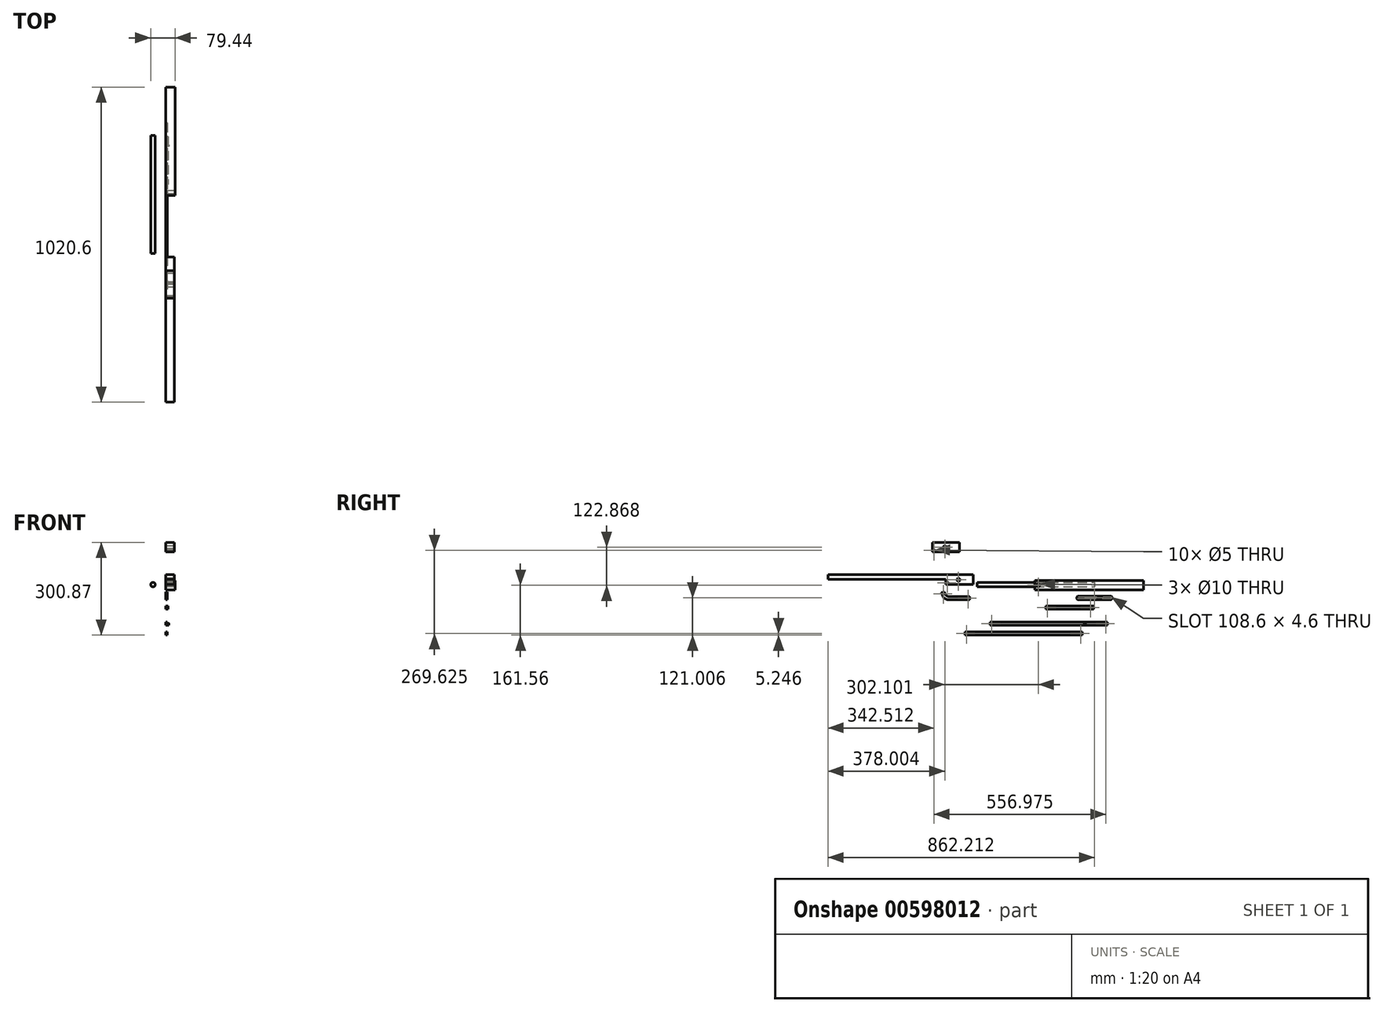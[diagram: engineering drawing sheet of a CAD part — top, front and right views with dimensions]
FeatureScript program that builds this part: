
annotation { "Feature Type Name" : "Feature", "Feature Type Description" : "" }
export const myFeature = defineFeature(function(context is Context, id is Id, definition is map)
    precondition{}
    {
        {
            var Q0;
            Q0=qCreatedBy(makeId("Right.planeOp"),FACE);
            var sketch = newSketch(context, id + "F0", { "sketchPlane" : qUnion([Q0])});
            skLineSegment(sketch, "E0.bottom", {"start": v(-194.1, 14.75) * mm, "end": v(156.9, 14.75) * mm});
            skLineSegment(sketch, "E0.top", {"start": v(-194.1, 44.75) * mm, "end": v(156.9, 44.75) * mm});
            skLineSegment(sketch, "E0.left", {"start": v(-194.1, 14.75) * mm, "end": v(-194.1, 44.75) * mm});
            skLineSegment(sketch, "E0.right", {"start": v(156.9, 14.75) * mm, "end": v(156.9, 44.75) * mm});
            skCircle(sketch, "E1", {"center": v(-183.6, 29.75) * mm, "radius": 5 * mm});
            skSolve(sketch);
        }
        {
            var Q0;
            Q0=qCreatedBy(makeId("Right.planeOp"),FACE);
            var sketch = newSketch(context, id + "F1", { "sketchPlane" : qUnion([Q0])});
            skCircle(sketch, "E2", {"center": v(-441.72, 47.74) * mm, "radius": 5 * mm});
            skLineSegment(sketch, "E3.bottom", {"start": v(-482.2, 64.18) * mm, "end": v(-393.7, 64.18) * mm});
            skLineSegment(sketch, "E3.top", {"start": v(-482.2, 33.18) * mm, "end": v(-393.7, 33.18) * mm});
            skLineSegment(sketch, "E3.left", {"start": v(-482.2, 64.18) * mm, "end": v(-482.2, 33.18) * mm});
            skLineSegment(sketch, "E3.right", {"start": v(-393.7, 64.18) * mm, "end": v(-393.7, 33.18) * mm});
            skCircle(sketch, "E4", {"center": v(-477.2, 38.18) * mm, "radius": 2.5 * mm});
            skLineSegment(sketch, "E5", {"start": v(-482.2, 64.18) * mm, "end": v(-863.7, 64.18) * mm});
            skLineSegment(sketch, "E6", {"start": v(-863.7, 64.18) * mm, "end": v(-863.7, 49.18) * mm});
            skLineSegment(sketch, "E7", {"start": v(-863.7, 49.18) * mm, "end": v(-482.2, 49.18) * mm});
            skSolve(sketch);
        }
        {
            var Q0;
            Q0=qCreatedBy(makeId("Right.planeOp"),FACE);
            var sketch = newSketch(context, id + "F2", { "sketchPlane" : qUnion([Q0])});
            skCircle(sketch, "E8", {"center": v(-410.94, -12.13) * mm, "radius": 2.5 * mm});
            skCircle(sketch, "E9", {"center": v(-490.17, 2.37) * mm, "radius": 2.5 * mm});
            skLineSegment(sketch, "E10.bottom", {"start": v(-468.94, -6.88) * mm, "end": v(-405.94, -6.88) * mm});
            skLineSegment(sketch, "E10.top", {"start": v(-468.94, -17.38) * mm, "end": v(-405.94, -17.38) * mm});
            skLineSegment(sketch, "E10.left", {"start": v(-468.94, -6.88) * mm, "end": v(-468.94, -17.38) * mm});
            skLineSegment(sketch, "E10.right", {"start": v(-405.94, -6.88) * mm, "end": v(-405.94, -17.38) * mm});
            skFitSpline(sketch, "E11", {"points": [v(-468.94, -6.88) * mm, v(-480.44, -3.93) * mm, v(-486.77, 8.58) * mm], "startDerivative": vector(-26.1, 0) * mm, "endDerivative": vector(-7.25, 24.7) * mm});
            skFitSpline(sketch, "E12.0", {"points": [v(-468.94, -17.38) * mm, v(-469.56, -17.38) * mm, v(-470.86, -17.37) * mm, v(-472.98, -17.27) * mm, v(-475.24, -17.03) * mm, v(-477.66, -16.6) * mm, v(-479.79, -16.03) * mm, v(-481.54, -15.38) * mm, v(-482.88, -14.79) * mm, v(-484.22, -14.08) * mm, v(-485.54, -13.25) * mm, v(-486.62, -12.46) * mm, v(-487.46, -11.75) * mm, v(-488.26, -11.02) * mm, v(-489.16, -10.1) * mm, v(-490.45, -8.58) * mm, v(-491.79, -6.66) * mm, v(-493.08, -4.4) * mm, v(-494.13, -2.18) * mm, v(-495, -0.04) * mm, v(-495.72, 2) * mm, v(-496.33, 3.9) * mm, v(-496.68, 5.07) * mm, v(-496.84, 5.62) * mm]});
            skLineSegment(sketch, "E13", {"start": v(-496.84, 5.62) * mm, "end": v(-486.77, 8.58) * mm});
            skSolve(sketch);
        }
        {
            var Q0;
            Q0=qCreatedBy(makeId("Right.planeOp"),FACE);
            var sketch = newSketch(context, id + "F3", { "sketchPlane" : qUnion([Q0])});
            skLineSegment(sketch, "E14.bottom", {"start": v(-3.79, -47.36) * mm, "end": v(-158.79, -47.36) * mm});
            skLineSegment(sketch, "E14.top", {"start": v(-3.79, -36.86) * mm, "end": v(-158.79, -36.86) * mm});
            skLineSegment(sketch, "E14.left", {"start": v(-3.79, -47.36) * mm, "end": v(-3.79, -36.86) * mm});
            skLineSegment(sketch, "E14.right", {"start": v(-158.79, -47.36) * mm, "end": v(-158.79, -36.86) * mm});
            skPoint(sketch, "E15.visualSharp", {"position": v(-3.79, -36.36) * mm});
            skPoint(sketch, "E16.visualSharp", {"position": v(-3.79, -47.36) * mm});
            skCircle(sketch, "E17", {"center": v(-153.79, -42.1) * mm, "radius": 2.5 * mm});
            skCircle(sketch, "E18", {"center": v(-13.79, -42.1) * mm, "radius": 2.5 * mm});
            skPoint(sketch, "E19", {"position": v(-3.79, -36.86) * mm});
            skSolve(sketch);
        }
        {
            var Q0;
            Q0=qCreatedBy(makeId("Right.planeOp"),FACE);
            var sketch = newSketch(context, id + "F4", { "sketchPlane" : qUnion([Q0])});
            skLineSegment(sketch, "E20.bottom", {"start": v(-54.3, -5.58) * mm, "end": v(51.4, -5.58) * mm});
            skLineSegment(sketch, "E20.top", {"start": v(-54.4, -16.58) * mm, "end": v(51.4, -16.58) * mm});
            skLineSegment(sketch, "E20.left", {"start": v(-59, -10.28) * mm, "end": v(-59, -11.98) * mm});
            skLineSegment(sketch, "E20.right", {"start": v(56, -10.18) * mm, "end": v(56, -11.98) * mm});
            skLineSegment(sketch, "E21", {"start": v(-53.5, -10.8) * mm, "end": v(50.5, -10.8) * mm});
            skPoint(sketch, "E22.visualSharp", {"position": v(-59, -5.58) * mm});
            skArc(sketch, "E22.filletArc", {"start": v(-54.3, -5.58) * mm, "mid": v(-57.62, -6.95) * mm, "end": v(-59, -10.28) * mm});
            skPoint(sketch, "E23.visualSharp", {"position": v(-59, -16.58) * mm});
            skArc(sketch, "E23.filletArc", {"start": v(-59, -11.98) * mm, "mid": v(-57.65, -15.23) * mm, "end": v(-54.4, -16.58) * mm});
            skPoint(sketch, "E24.visualSharp", {"position": v(56, -16.58) * mm});
            skArc(sketch, "E24.filletArc", {"start": v(51.4, -16.58) * mm, "mid": v(54.65, -15.23) * mm, "end": v(56, -11.98) * mm});
            skPoint(sketch, "E25.visualSharp", {"position": v(56, -5.58) * mm});
            skArc(sketch, "E25.filletArc", {"start": v(56, -10.18) * mm, "mid": v(54.65, -6.92) * mm, "end": v(51.4, -5.58) * mm});
            skArc(sketch, "E26.0.startCap", {"start": v(-53.5, -13.1) * mm, "mid": v(-55.8, -10.8) * mm, "end": v(-53.5, -8.5) * mm});
            skArc(sketch, "E26.0.endCap", {"start": v(50.5, -8.5) * mm, "mid": v(52.8, -10.8) * mm, "end": v(50.5, -13.1) * mm});
            skLineSegment(sketch, "E26.0.left", {"start": v(-53.5, -8.5) * mm, "end": v(50.5, -8.5) * mm});
            skLineSegment(sketch, "E26.0.right", {"start": v(-53.5, -13.1) * mm, "end": v(50.5, -13.1) * mm});
            skPoint(sketch, "E27", {"position": v(-59, -6.08) * mm});
            skSolve(sketch);
        }
        {
            var Q0;
            Q0=makeQuery(id+"F0.imprint","IMPRINT",FACE,{"disambiguationData":[TD([[makeQuery(id+"F0.imprint","IMPRINT",EDGE,{"derivedFrom":sQuery(id+"F0.wireOp",EDGE,"E0.bottom")}),1.0]])]});
            extrude(context, id + "F5", {"entities" : qUnion([Q0]), "depth" : 30 * mm, "offsetDistance" : 25 * mm});
        }
        {
            var Q0;
            Q0 = qSketchRegion(id + "F1", true);
            extrude(context, id + "F6", {"entities" : qUnion([Q0]), "depth" : 28 * mm, "offsetDistance" : 25 * mm});
        }
        {
            var Q0;
            Q0 = qSketchRegion(id + "F2", true);
            extrude(context, id + "F7", {"entities" : qUnion([Q0]), "depth" : 5 * mm, "offsetDistance" : 25 * mm});
        }
        {
            var Q0;
            Q0 = qSketchRegion(id + "F3", true);
            extrude(context, id + "F8", {"entities" : qUnion([Q0]), "depth" : 7 * mm, "offsetDistance" : 25 * mm});
        }
        {
            var Q0;
            Q0 = qSketchRegion(id + "F4", true);
            extrude(context, id + "F9", {"entities" : qUnion([Q0]), "depth" : 2 * mm, "offsetDistance" : 25 * mm});
        }
        {
            var Q0;
            Q0=qCreatedBy(makeId("Right.planeOp"),FACE);
            var sketch = newSketch(context, id + "F10", { "sketchPlane" : qUnion([Q0])});
            skCircle(sketch, "E28", {"center": v(-32.9, -96.73) * mm, "radius": 2.5 * mm});
            skSolve(sketch);
        }
        {
            var Q0;
            Q0=makeQuery(id+"F10.imprint","IMPRINT",FACE,{"disambiguationData":[TD([[makeQuery(id+"F10.imprint","IMPRINT",EDGE,{"derivedFrom":sQuery(id+"F10.wireOp",EDGE,"E28")}),1.0]])]});
            extrude(context, id + "F11", {"entities" : qUnion([Q0]), "depth" : 10 * mm, "offsetDistance" : 25 * mm});
        }
        {
            var Q0;
            Q0=qCreatedBy(makeId("Right.planeOp"),FACE);
            var sketch = newSketch(context, id + "F12", { "sketchPlane" : qUnion([Q0])});
            skLineSegment(sketch, "E29.bottom", {"start": v(40.78, -99.32) * mm, "end": v(-339.22, -99.32) * mm});
            skLineSegment(sketch, "E29.top", {"start": v(40.78, -88.82) * mm, "end": v(-339.22, -88.82) * mm});
            skLineSegment(sketch, "E29.left", {"start": v(40.78, -99.32) * mm, "end": v(40.78, -88.82) * mm});
            skLineSegment(sketch, "E29.right", {"start": v(-339.22, -99.32) * mm, "end": v(-339.22, -88.82) * mm});
            skPoint(sketch, "E30.visualSharp", {"position": v(-184.22, -88.32) * mm});
            skPoint(sketch, "E31.visualSharp", {"position": v(40.78, -99.32) * mm});
            skCircle(sketch, "E32", {"center": v(-334.22, -94.07) * mm, "radius": 2.5 * mm});
            skCircle(sketch, "E33", {"center": v(35.78, -94.07) * mm, "radius": 2.5 * mm});
            skPoint(sketch, "E34", {"position": v(40.78, -88.82) * mm});
            skSolve(sketch);
        }
        {
            var Q0;
            Q0=makeQuery(id+"F12.imprint","IMPRINT",FACE,{"disambiguationData":[TD([[makeQuery(id+"F12.imprint","IMPRINT",EDGE,{"derivedFrom":sQuery(id+"F12.wireOp",EDGE,"E29.bottom")}),-1.0]])]});
            extrude(context, id + "F13", {"entities" : qUnion([Q0]), "operationType" : NewBodyOperationType.ADD, "depth" : 4 * mm, "offsetDistance" : 25 * mm});
        }
        {
            var Q0;
            Q0=qCreatedBy(makeId("Right.planeOp"),FACE);
            var sketch = newSketch(context, id + "F14", { "sketchPlane" : qUnion([Q0])});
            skLineSegment(sketch, "E35.bottom", {"start": v(-40.78, -131.81) * mm, "end": v(-420.78, -131.81) * mm});
            skLineSegment(sketch, "E35.top", {"start": v(-40.78, -121.31) * mm, "end": v(-420.78, -121.31) * mm});
            skLineSegment(sketch, "E35.left", {"start": v(-40.78, -131.81) * mm, "end": v(-40.78, -121.31) * mm});
            skLineSegment(sketch, "E35.right", {"start": v(-420.78, -131.81) * mm, "end": v(-420.78, -121.31) * mm});
            skPoint(sketch, "E36.visualSharp", {"position": v(-265.78, -120.81) * mm});
            skPoint(sketch, "E37.visualSharp", {"position": v(-40.78, -131.81) * mm});
            skCircle(sketch, "E38", {"center": v(-415.78, -126.56) * mm, "radius": 2.5 * mm});
            skCircle(sketch, "E39", {"center": v(-45.78, -126.56) * mm, "radius": 2.5 * mm});
            skPoint(sketch, "E40", {"position": v(-40.78, -121.31) * mm});
            skSolve(sketch);
        }
        {
            var Q0;
            Q0=makeQuery(id+"F14.imprint","IMPRINT",FACE,{"disambiguationData":[TD([[makeQuery(id+"F14.imprint","IMPRINT",EDGE,{"derivedFrom":sQuery(id+"F14.wireOp",EDGE,"E35.bottom")}),-1.0]])]});
            extrude(context, id + "F15", {"entities" : qUnion([Q0]), "depth" : 4 * mm, "offsetDistance" : 25 * mm});
        }
        {
            var Q0;
            Q0=qCreatedBy(makeId("Right.planeOp"),FACE);
            var sketch = newSketch(context, id + "F16", { "sketchPlane" : qUnion([Q0])});
            skCircle(sketch, "E41", {"center": v(-485.7, 152.62) * mm, "radius": 5 * mm});
            skLineSegment(sketch, "E42.bottom", {"start": v(-526.2, 169.06) * mm, "end": v(-437.7, 169.06) * mm});
            skLineSegment(sketch, "E42.top", {"start": v(-526.2, 138.06) * mm, "end": v(-437.7, 138.06) * mm});
            skLineSegment(sketch, "E42.left", {"start": v(-526.2, 169.06) * mm, "end": v(-526.2, 138.06) * mm});
            skLineSegment(sketch, "E42.right", {"start": v(-437.7, 169.06) * mm, "end": v(-437.7, 138.06) * mm});
            skCircle(sketch, "E43", {"center": v(-521.2, 143.06) * mm, "radius": 2.5 * mm});
            skSolve(sketch);
        }
        {
            var Q0;
            Q0=qCreatedBy(makeId("Front.planeOp"),FACE);
            var sketch = newSketch(context, id + "F17", { "sketchPlane" : qUnion([Q0])});
            skCircle(sketch, "E44", {"center": v(-41.94, 31.86) * mm, "radius": 7.5 * mm});
            skSolve(sketch);
        }
        {
            var Q0;
            Q0=makeQuery(id+"F17.imprint","IMPRINT",FACE,{"disambiguationData":[TD([[makeQuery(id+"F17.imprint","IMPRINT",EDGE,{"derivedFrom":sQuery(id+"F17.wireOp",EDGE,"E44")}),1.0]])]});
            var Q1;
            Q1=sQuery(id+"F17.wireOp",EDGE,"E44");
            extrude(context, id + "F18", {"entities" : qUnion([Q0]), "surfaceEntities" : qUnion([Q1]), "depth" : 381.5 * mm, "offsetDistance" : 25 * mm});
        }
        {
            var Q0;
            Q0=makeQuery(id+"F16.imprint","IMPRINT",FACE,{"disambiguationData":[TD([[makeQuery(id+"F16.imprint","IMPRINT",EDGE,{"derivedFrom":sQuery(id+"F16.wireOp",EDGE,"E41")}),-1.0]])]});
            extrude(context, id + "F19", {"entities" : qUnion([Q0]), "depth" : 28 * mm, "offsetDistance" : 25 * mm});
        }
    });
